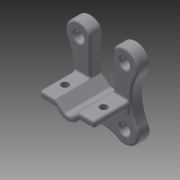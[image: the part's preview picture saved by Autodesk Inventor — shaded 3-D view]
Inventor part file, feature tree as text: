
AUTODESK INVENTOR PART (.ipt)
format: ipt  version: 2014 (Build 180170000, 170)  size: 411,648 bytes
history: native  units: in
note: dims shown in document units (in); Inventor stores cm internally (conversion verified against a paired STEP export)
features: fillet x5, extrude x4, sketch x4, chamfer x1
ambient origin geometry x8: Origin, YZ Plane, XZ Plane, XY Plane, X Axis, Y Axis, Z Axis, Center Point
bodies: Solid1 (feature_tree)
feature tree (14):
  extrude  "Extrusion1"  Depth=0.7874in
  extrude  "Extrusion2"  Depth=0.1575in
  extrude  "Extrusion3"  Depth=0.7874in
  extrude  "Extrusion4"  Depth=0.315in
  chamfer  "Chamfer1"  Distance=0.0394in
  fillet  "Fillet2"  Radius=0.1181in
  fillet  "Fillet1"  Radius=0.9449in
  fillet  "Fillet3"  Radius=0.0787in
  fillet  "Fillet4"  Radius=0.1319in
  fillet  "Fillet5"  Radius=0.2165in
  sketch  "Sketch1"  dims[d0=0.9843in d1=0.7874in]
  sketch  "Sketch2"  dims[d2=0.1516in d3=0.1575in]
  sketch  "Sketch3"  dims[d4=0.5906in d5=0.7874in]
  sketch  "Sketch4"  dims[d6=0.1969in d7=0.0in d8=0.315in d9=0.0394in d10=0.1181in d11=0.9449in d12=0.0787in d13=0.1319in d14=0.2165in d15=0.0984in d16=0.5906in d17=0.0in d18=0.126in d19=0.5906in d20=0.0in d21=0.0787in d22=0.0787in d23=45.0deg d24=0.0394in d25=0.3937in d26=0.0in d27=0.1181in d28=0.0394in d29=0.0394in d30=0.0394in]
